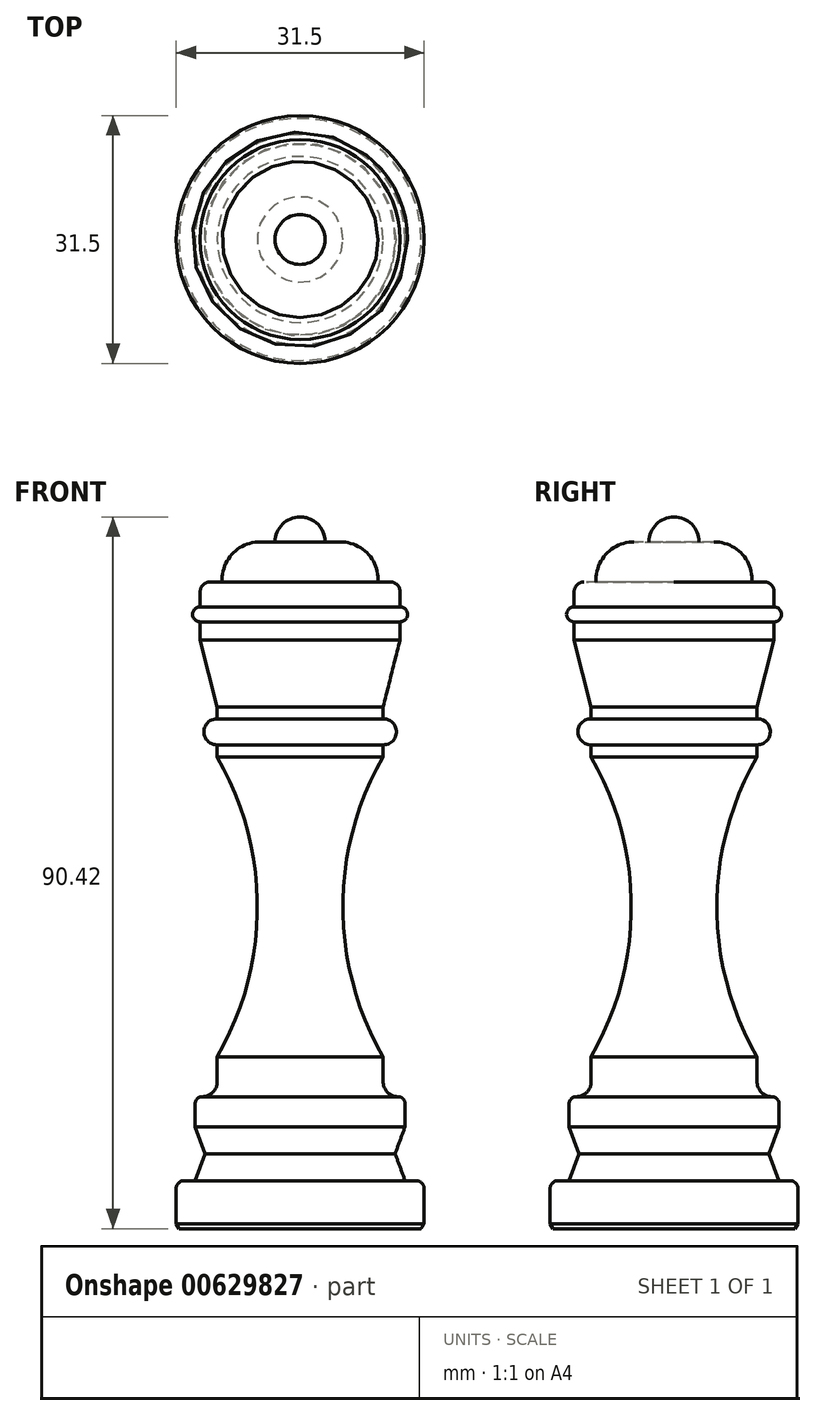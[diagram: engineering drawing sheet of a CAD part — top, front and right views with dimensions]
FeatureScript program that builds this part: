
annotation { "Feature Type Name" : "Feature", "Feature Type Description" : "" }
export const myFeature = defineFeature(function(context is Context, id is Id, definition is map)
    precondition{}
    {
        {
            var Q0;
            Q0=qCreatedBy(makeId("Front.planeOp"),FACE);
            var sketch = newSketch(context, id + "F0", { "sketchPlane" : qUnion([Q0])});
            skPoint(sketch, "E0.middle", {"position": v(0, 0) * mm});
            skLineSegment(sketch, "E1.MirrorCS", {"start": v(15.37, -3.73) * mm, "end": v(15.75, -3.1) * mm});
            skLineSegment(sketch, "E2.MirrorCS", {"start": v(15.37, -3.73) * mm, "end": v(0, -3.73) * mm});
            skLineSegment(sketch, "E3", {"start": v(15.75, -3.1) * mm, "end": v(15.75, 1.35) * mm});
            skArc(sketch, "E4", {"start": v(15.75, 1.35) * mm, "mid": v(15.45, 2.07) * mm, "end": v(14.73, 2.37) * mm});
            skLineSegment(sketch, "E5", {"start": v(14.73, 2.37) * mm, "end": v(13.34, 2.37) * mm});
            skLineSegment(sketch, "E6", {"start": v(13.34, 2.37) * mm, "end": v(12.07, 5.8) * mm});
            skLineSegment(sketch, "E7", {"start": v(12.07, 5.8) * mm, "end": v(13.34, 9.22) * mm});
            skLineSegment(sketch, "E8", {"start": v(13.34, 9.22) * mm, "end": v(13.34, 12.14) * mm});
            skArc(sketch, "E9", {"start": v(13.34, 12.14) * mm, "mid": v(13.07, 12.77) * mm, "end": v(12.45, 13.03) * mm});
            skArc(sketch, "E10", {"start": v(10.54, 14.94) * mm, "mid": v(11.1, 13.6) * mm, "end": v(12.45, 13.03) * mm});
            skLineSegment(sketch, "E11", {"start": v(10.54, 14.94) * mm, "end": v(10.54, 18.11) * mm});
            skLineSegment(sketch, "E12", {"start": v(10.54, 62.56) * mm, "end": v(12.7, 71.07) * mm});
            skArc(sketch, "E13", {"start": v(12.7, 77.17) * mm, "mid": v(12.33, 78.07) * mm, "end": v(11.43, 78.44) * mm});
            skLineSegment(sketch, "E14", {"start": v(11.43, 78.44) * mm, "end": v(9.9, 78.44) * mm});
            skArc(sketch, "E15", {"start": v(9.9, 78.44) * mm, "mid": v(8.58, 82.01) * mm, "end": v(5.08, 83.52) * mm});
            skLineSegment(sketch, "E16", {"start": v(5.08, 83.52) * mm, "end": v(3.18, 83.52) * mm});
            skArc(sketch, "E17", {"start": v(3.18, 83.52) * mm, "mid": v(2.25, 85.76) * mm, "end": v(0, 86.7) * mm});
            skArc(sketch, "E18", {"start": v(10.54, 56.21) * mm, "mid": v(5.44, 37.16) * mm, "end": v(10.54, 18.11) * mm});
            skLineSegment(sketch, "E19", {"start": v(0, 86.7) * mm, "end": v(0, -3.73) * mm});
            skArc(sketch, "E20", {"start": v(12.7, 73.36) * mm, "mid": v(13.65, 74.31) * mm, "end": v(12.7, 75.26) * mm});
            skLineSegment(sketch, "E21", {"start": v(12.7, 77.17) * mm, "end": v(12.7, 75.26) * mm});
            skLineSegment(sketch, "E22", {"start": v(12.7, 73.36) * mm, "end": v(12.7, 71.07) * mm});
            skLineSegment(sketch, "E23", {"start": v(10.54, 62.56) * mm, "end": v(10.54, 61.04) * mm});
            skLineSegment(sketch, "E24", {"start": v(10.54, 56.21) * mm, "end": v(10.54, 57.74) * mm});
            skArc(sketch, "E25", {"start": v(10.54, 57.74) * mm, "mid": v(12.22, 59.39) * mm, "end": v(10.54, 61.04) * mm});
            skSolve(sketch);
        }
        {
            var Q0;
            Q0=makeQuery(id+"F0.imprint","IMPRINT",FACE,{"disambiguationData":[TD([[makeQuery(id+"F0.imprint","IMPRINT",EDGE,{"derivedFrom":sQuery(id+"F0.wireOp",EDGE,"E1.MirrorCS")}),1.0]])]});
            var Q1;
            Q1=sQuery(id+"F0.wireOp",EDGE,"E19");
            revolve(context, id + "F1", {"entities" : qUnion([Q0]), "axis" : qUnion([Q1]), "revolveType" : RevolveType.FULL});
        }
    });
